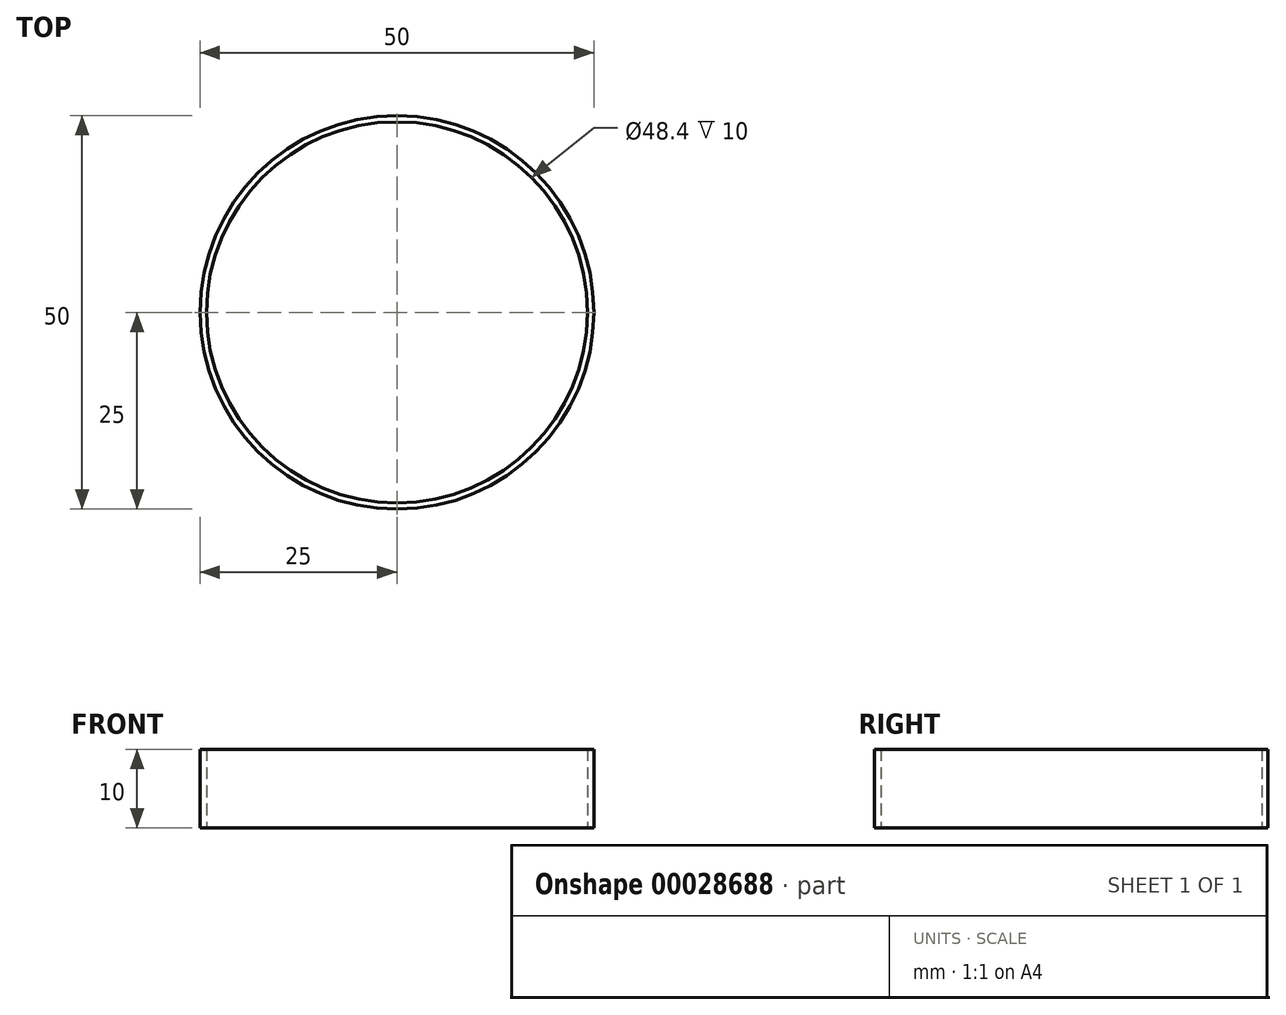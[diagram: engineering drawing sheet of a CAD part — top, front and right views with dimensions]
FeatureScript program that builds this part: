
annotation { "Feature Type Name" : "Feature", "Feature Type Description" : "" }
export const myFeature = defineFeature(function(context is Context, id is Id, definition is map)
    precondition{}
    {
        {
            var Q0;
            Q0=qCreatedBy(makeId("Top.planeOp"),FACE);
            var sketch = newSketch(context, id + "F0", { "sketchPlane" : qUnion([Q0])});
            skCircle(sketch, "E0", {"center": v(0, 0) * mm, "radius": 25 * mm});
            skCircle(sketch, "E1", {"center": v(0, 0) * mm, "radius": 24.2 * mm});
            skSolve(sketch);
        }
        {
            var Q0;
            Q0 = qSketchRegion(id + "F0", true);
            extrude(context, id + "F1", {"entities" : qUnion([Q0]), "depth" : 10 * mm});
        }
    });
